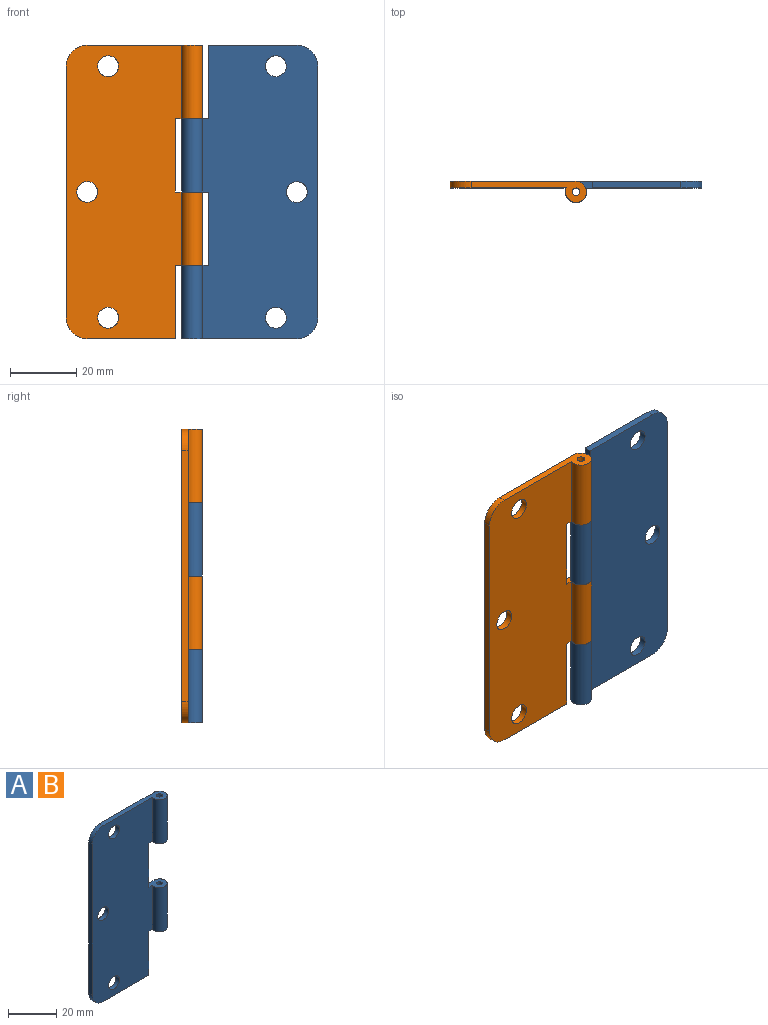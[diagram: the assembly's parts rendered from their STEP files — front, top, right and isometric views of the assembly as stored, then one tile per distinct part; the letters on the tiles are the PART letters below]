
ASSEMBLY  parts=2 mates=1
PART A: 19 faces, bbox 41.3x6.4x88.9 mm
  f0: plane 88.9x38.1mm, normal (0,1,0), area 3049mm2, adj f3,f4,f5,f6,f7,f8,f9,f10
  f1: plane 88.9x35.14mm, normal (0,-1,0), area 2917.3mm2, adj f3,f4,f5,f6,f7,f8,f9,f10
  f2: cylinder r=1.14mm len=22.23mm, axis (0,0,-1), area 159.6mm2, adj f7,f12
  f3: cylinder r=3.17mm len=22.23mm, axis (0,0,-1), area 358.5mm2, adj f0,f1,f7,f12
  f4: plane 26.67x2.03mm, normal (0,0,-1), area 54.2mm2, adj f0,f1,f8,f14
  f5: plane 76.2x2.03mm, normal (-1,0,0), area 154.8mm2, adj f0,f1,f8,f9
  f6: cylinder r=3.17mm len=22.23mm, axis (0,0,-1), area 358.5mm2, adj f0,f1,f11,f13
  f7: plane 34.93x6.35mm, normal (0,0,1), area 87.7mm2, adj f0,f1,f2,f3,f9
  f8: cylinder r=6.35mm len=6.35mm, axis (0,-1,0), area 20.3mm2, adj f0,f1,f4,f5
  f9: cylinder r=6.35mm len=6.35mm, axis (0,1,0), area 20.3mm2, adj f0,f1,f5,f7
  f10: plane 22.23x2.03mm, normal (1,0,0), area 45.2mm2, adj f0,f1,f11,f12
  f11: plane 8.26x6.35mm, normal (0,0,1), area 33.5mm2, adj f0,f1,f6,f10,f15
  f12: plane 8.26x6.35mm, normal (0,0,-1), area 33.5mm2, adj f0,f1,f2,f3,f10
  f13: plane 8.26x6.35mm, normal (0,0,-1), area 33.5mm2, adj f0,f1,f6,f14,f15
  f14: plane 22.23x2.03mm, normal (1,0,0), area 45.2mm2, adj f0,f1,f4,f13
  f15: cylinder r=1.14mm len=22.23mm, axis (0,0,-1), area 159.6mm2, adj f11,f13
  f16: cylinder r=3.17mm len=6.35mm, axis (0,1,0), area 40.5mm2, adj f0,f1
  f17: cylinder r=3.17mm len=6.35mm, axis (0,1,0), area 40.5mm2, adj f0,f1
  f18: cylinder r=3.17mm len=6.35mm, axis (0,1,0), area 40.5mm2, adj f0,f1
PART B: same geometry as A
PLACE A rot(axis=(0,1,0),180deg) t=(76.2,0,88.9)mm
PLACE B at identity fixed
MATE revolute A.f2 <-> B.f2  axis (0,0,1) through (38.1,-3.18,44.45)mm
